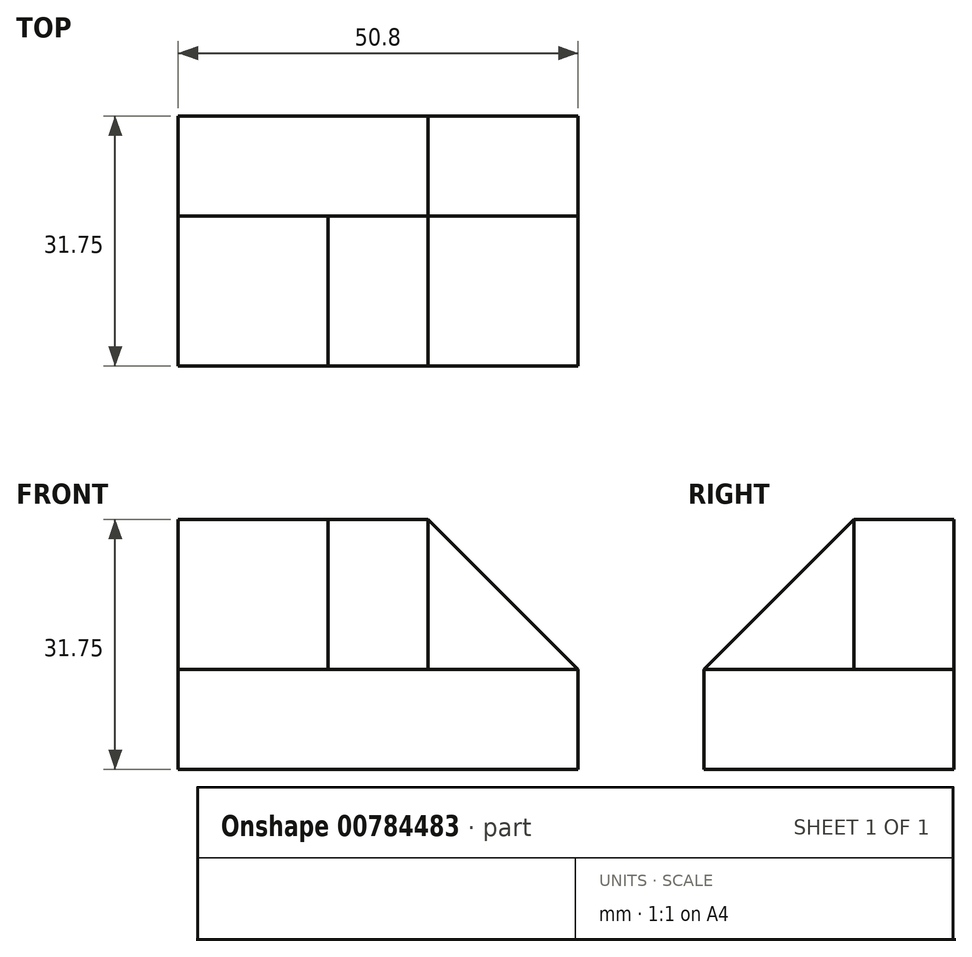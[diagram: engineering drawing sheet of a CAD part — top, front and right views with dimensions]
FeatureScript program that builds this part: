
annotation { "Feature Type Name" : "Feature", "Feature Type Description" : "" }
export const myFeature = defineFeature(function(context is Context, id is Id, definition is map)
    precondition{}
    {
        {
            var Q0;
            Q0=qCreatedBy(makeId("Front.planeOp"),FACE);
            var sketch = newSketch(context, id + "F0", { "sketchPlane" : qUnion([Q0])});
            skLineSegment(sketch, "E0", {"start": v(0, 0) * mm, "end": v(50.8, 0) * mm});
            skLineSegment(sketch, "E1", {"start": v(50.8, 0) * mm, "end": v(50.8, 31.75) * mm});
            skLineSegment(sketch, "E2", {"start": v(50.8, 31.75) * mm, "end": v(0, 31.75) * mm});
            skLineSegment(sketch, "E3", {"start": v(0, 0) * mm, "end": v(0, 31.75) * mm});
            skSolve(sketch);
        }
        {
            var Q0;
            Q0=makeQuery(id+"F0.imprint","IMPRINT",FACE,{"disambiguationData":[TD([[makeQuery(id+"F0.imprint","IMPRINT",EDGE,{"derivedFrom":sQuery(id+"F0.wireOp",EDGE,"E0")}),1.0]])]});
            extrude(context, id + "F1", {"entities" : qUnion([Q0]), "depth" : 31.75 * mm, "offsetDistance" : 25.4 * mm});
        }
        {
            var Q0;
            Q0=makeQuery(id+"F1.opExtrude","CAP_FACE",FACE,{"disambiguationData":[OSD([sQuery(id+"F0.wireOp",EDGE,"E0"),sQuery(id+"F0.wireOp",EDGE,"E1"),sQuery(id+"F0.wireOp",EDGE,"E2"),sQuery(id+"F0.wireOp",EDGE,"E3")])],"isStart":false});
            var sketch = newSketch(context, id + "F2", { "sketchPlane" : qUnion([Q0])});
            skLineSegment(sketch, "E4", {"start": v(0, 0) * mm, "end": v(0, 12.7) * mm});
            skLineSegment(sketch, "E5", {"start": v(0, 12.7) * mm, "end": v(19.05, 12.7) * mm});
            skLineSegment(sketch, "E6", {"start": v(19.05, 12.7) * mm, "end": v(19.05, 31.75) * mm});
            skLineSegment(sketch, "E7", {"start": v(50.8, 0) * mm, "end": v(50.8, 12.7) * mm});
            skLineSegment(sketch, "E8", {"start": v(50.8, 12.7) * mm, "end": v(31.75, 12.7) * mm});
            skLineSegment(sketch, "E9", {"start": v(31.75, 12.7) * mm, "end": v(31.75, 31.75) * mm});
            skSolve(sketch);
        }
        {
            var Q0;
            {var subQ0=sQuery(id+"F2.wireOp",EDGE,"E8");Q0=makeQuery(id+"F2.imprint","IMPRINT",FACE,{"disambiguationData":[TD([[makeQuery(id+"F2.imprint","IMPRINT",EDGE,{"derivedFrom":subQ0}),-1.0]])]});}
            extrude(context, id + "F3", {"entities" : qUnion([Q0]), "operationType" : NewBodyOperationType.REMOVE, "oppositeDirection" : true, "depth" : 19.05 * mm, "offsetDistance" : 25.4 * mm});
        }
        {
            var Q0;
            {var subQ0=sQuery(id+"F2.wireOp",EDGE,"E5");Q0=makeQuery(id+"F2.imprint","IMPRINT",FACE,{"disambiguationData":[TD([[makeQuery(id+"F2.imprint","IMPRINT",EDGE,{"derivedFrom":subQ0}),1.0]])]});}
            extrude(context, id + "F4", {"entities" : qUnion([Q0]), "operationType" : NewBodyOperationType.REMOVE, "oppositeDirection" : true, "depth" : 19.05 * mm, "offsetDistance" : 25.4 * mm});
        }
        {
            var Q0;
            Q0=makeQuery(id+"F3.boolean.opBoolean","COPY",FACE,{"derivedFrom":makeQuery(id+"F3.opExtrude","SWEPT_FACE",FACE,{"disambiguationData":[OSD([sQuery(id+"F2.wireOp",EDGE,"E9")])]})});
            var sketch = newSketch(context, id + "F5", { "sketchPlane" : qUnion([Q0])});
            skLineSegment(sketch, "E10", {"start": v(-12.7, 31.75) * mm, "end": v(-31.75, 12.7) * mm});
            skSolve(sketch);
        }
        {
            var Q0;
            Q0=makeQuery(id+"F5.imprint","IMPRINT",FACE,{"disambiguationData":[TD([[makeQuery(id+"F5.imprint","IMPRINT",EDGE,{"derivedFrom":sQuery(id+"F5.wireOp",EDGE,"E10")}),-1.0]])]});
            extrude(context, id + "F6", {"entities" : qUnion([Q0]), "operationType" : NewBodyOperationType.REMOVE, "oppositeDirection" : true, "depth" : 12.7 * mm, "offsetDistance" : 25.4 * mm});
        }
        {
            var Q0;
            Q0=makeQuery(id+"F3.boolean.opBoolean","COPY",FACE,{"derivedFrom":makeQuery(id+"F3.opExtrude","CAP_FACE",FACE,{"disambiguationData":[OSD([sQuery(id+"F0.wireOp",EDGE,"E1"),sQuery(id+"F0.wireOp",EDGE,"E2"),sQuery(id+"F2.wireOp",EDGE,"E8"),sQuery(id+"F2.wireOp",EDGE,"E9")])],"isStart":false})});
            var sketch = newSketch(context, id + "F7", { "sketchPlane" : qUnion([Q0])});
            skLineSegment(sketch, "E11", {"start": v(31.75, 31.75) * mm, "end": v(50.8, 12.7) * mm});
            skSolve(sketch);
        }
        {
            var Q0;
            Q0=makeQuery(id+"F7.imprint","IMPRINT",FACE,{"disambiguationData":[TD([[makeQuery(id+"F7.imprint","IMPRINT",EDGE,{"derivedFrom":sQuery(id+"F7.wireOp",EDGE,"E11")}),1.0]])]});
            extrude(context, id + "F8", {"entities" : qUnion([Q0]), "operationType" : NewBodyOperationType.REMOVE, "oppositeDirection" : true, "depth" : 12.7 * mm, "offsetDistance" : 25.4 * mm});
        }
    });
